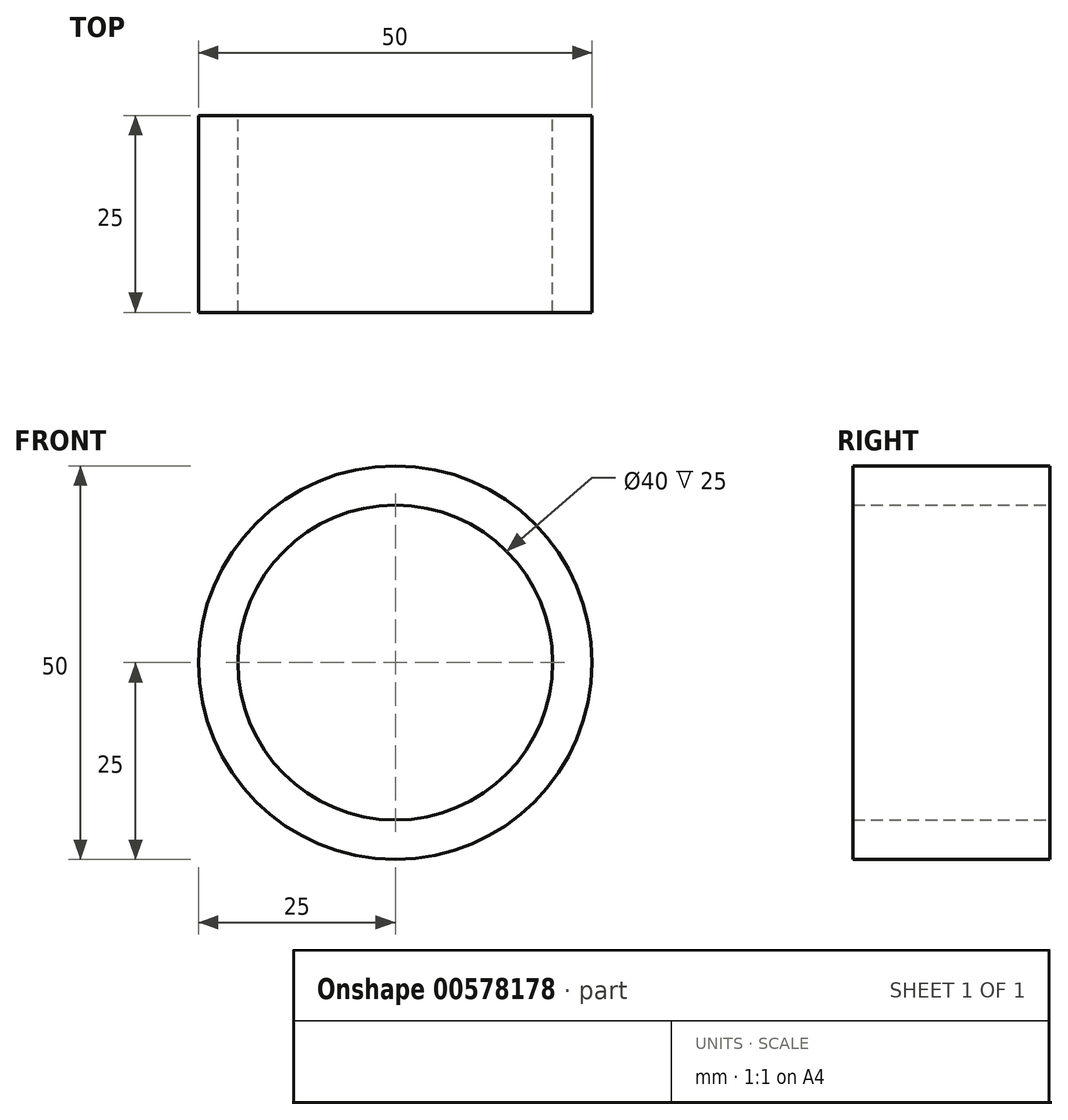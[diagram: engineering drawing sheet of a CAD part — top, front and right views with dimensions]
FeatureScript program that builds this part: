
annotation { "Feature Type Name" : "Feature", "Feature Type Description" : "" }
export const myFeature = defineFeature(function(context is Context, id is Id, definition is map)
    precondition{}
    {
        {
            var Q0;
            Q0=qCreatedBy(makeId("Front.planeOp"),FACE);
            var sketch = newSketch(context, id + "F0", { "sketchPlane" : qUnion([Q0])});
            skCircle(sketch, "E0", {"center": v(0, 0) * mm, "radius": 25 * mm});
            skCircle(sketch, "E1", {"center": v(0, 0) * mm, "radius": 20 * mm});
            skSolve(sketch);
        }
        {
            var Q0;
            Q0=makeQuery(id+"F0.imprint","IMPRINT",FACE,{"disambiguationData":[TD([[makeQuery(id+"F0.imprint","IMPRINT",EDGE,{"derivedFrom":sQuery(id+"F0.wireOp",EDGE,"E0")}),1.0]])]});
            extrude(context, id + "F1", {"entities" : qUnion([Q0]), "depth" : 25 * mm, "offsetDistance" : 25 * mm});
        }
    });
